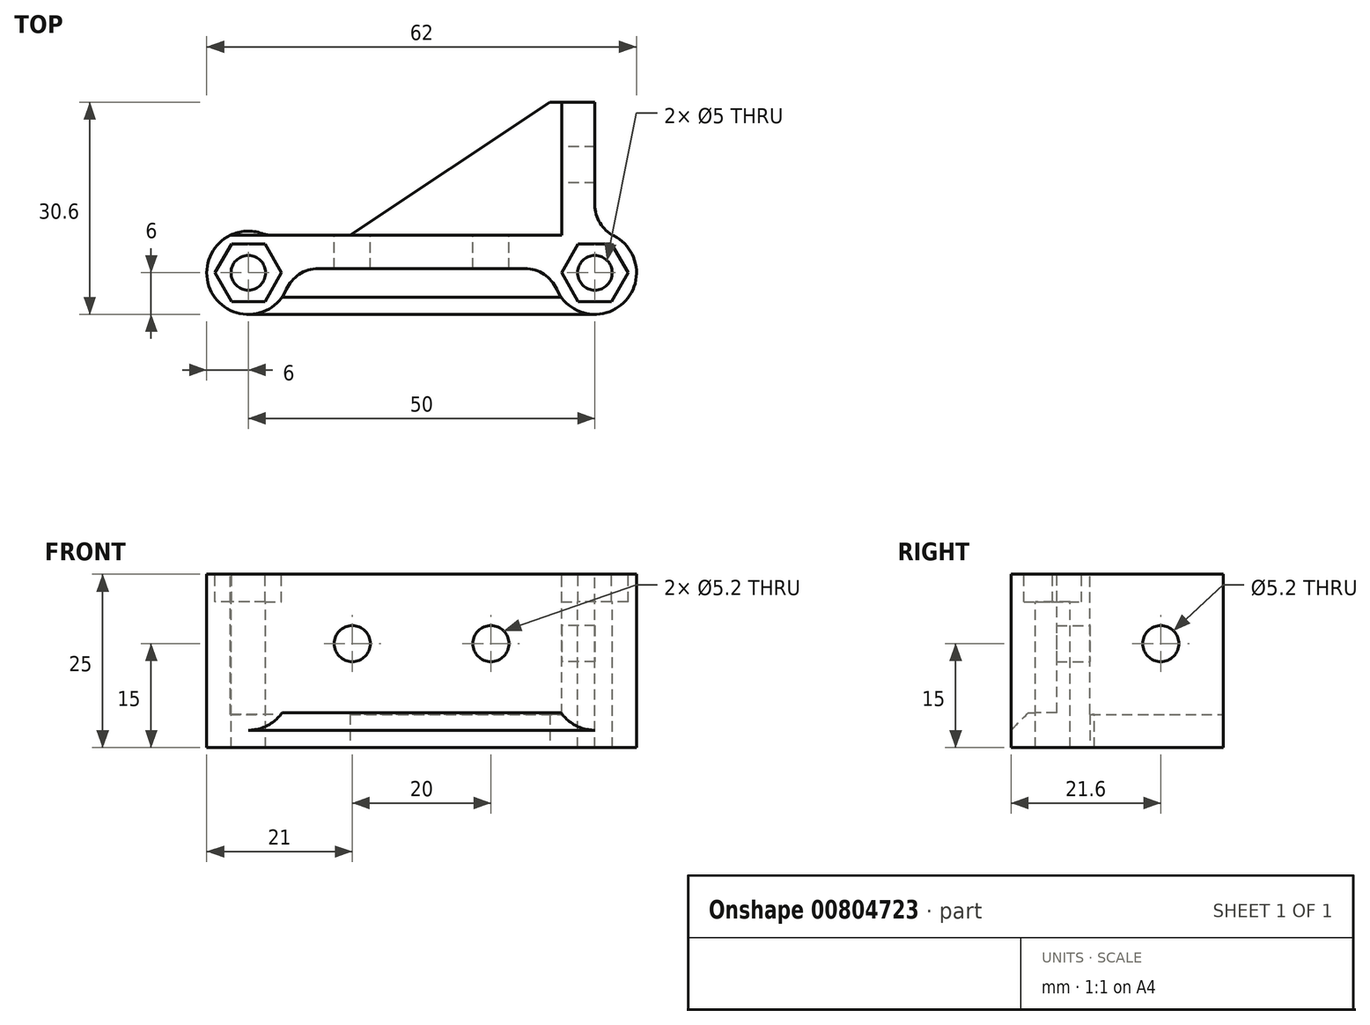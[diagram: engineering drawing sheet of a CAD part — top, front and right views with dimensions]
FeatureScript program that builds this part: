
annotation { "Feature Type Name" : "Feature", "Feature Type Description" : "" }
export const myFeature = defineFeature(function(context is Context, id is Id, definition is map)
    precondition{}
    {
        {
            var Q0;
            Q0=qCreatedBy(makeId("Top.planeOp"),FACE);
            var sketch = newSketch(context, id + "F0", { "sketchPlane" : qUnion([Q0])});
            skCircle(sketch, "E0", {"center": v(-25, 0) * mm, "radius": 2.5 * mm});
            skArc(sketch, "E1", {"start": v(-23.05, 5.67) * mm, "mid": v(-30.5, -2.41) * mm, "end": v(-19.5, -2.4) * mm});
            skCircle(sketch, "E2", {"center": v(25, 0) * mm, "radius": 2.5 * mm});
            skArc(sketch, "E3", {"start": v(19.5, -2.4) * mm, "mid": v(29.11, -4.37) * mm, "end": v(27.73, 5.34) * mm});
            skLineSegment(sketch, "E4", {"start": v(-21.42, 5.4) * mm, "end": v(20.2, 5.4) * mm});
            skLineSegment(sketch, "E5", {"start": v(-14.92, 0.6) * mm, "end": v(14.92, 0.6) * mm});
            skArc(sketch, "E6", {"start": v(-14.92, 0.6) * mm, "mid": v(-17.66, -0.22) * mm, "end": v(-19.5, -2.4) * mm});
            skArc(sketch, "E7", {"start": v(14.92, 0.6) * mm, "mid": v(17.66, -0.22) * mm, "end": v(19.5, -2.4) * mm});
            skLineSegment(sketch, "E8", {"start": v(20.2, 5.4) * mm, "end": v(20.2, 24.6) * mm});
            skLineSegment(sketch, "E9", {"start": v(20.2, 24.6) * mm, "end": v(25, 24.6) * mm});
            skLineSegment(sketch, "E10", {"start": v(25, 24.6) * mm, "end": v(25, 9.8) * mm});
            skArc(sketch, "E11", {"start": v(25, 9.8) * mm, "mid": v(25.74, 7.19) * mm, "end": v(27.73, 5.34) * mm});
            skLineSegment(sketch, "E12", {"start": v(-25, 0) * mm, "end": v(25, 0) * mm, "construction": true});
            skPoint(sketch, "E13.visualSharp", {"position": v(-22.38, 5.4) * mm});
            skArc(sketch, "E13.filletArc", {"start": v(-23.05, 5.67) * mm, "mid": v(-22.24, 5.47) * mm, "end": v(-21.42, 5.4) * mm});
            skSolve(sketch);
        }
        {
            var Q0;
            Q0=qSketchRegion(id+"F0",true);
            extrude(context, id + "F1", {"entities" : qUnion([Q0]), "oppositeDirection" : true, "depth" : 25 * mm, "offsetDistance" : 25 * mm});
        }
        {
            var Q0;
            Q0=makeQuery(id+"F1.opExtrude","CAP_FACE",FACE,{"disambiguationData":[OSD([sQuery(id+"F0.wireOp",EDGE,"E0"),sQuery(id+"F0.wireOp",EDGE,"E1"),sQuery(id+"F0.wireOp",EDGE,"E2"),sQuery(id+"F0.wireOp",EDGE,"E3"),sQuery(id+"F0.wireOp",EDGE,"E4"),sQuery(id+"F0.wireOp",EDGE,"E5"),sQuery(id+"F0.wireOp",EDGE,"E6"),sQuery(id+"F0.wireOp",EDGE,"E7"),sQuery(id+"F0.wireOp",EDGE,"E8"),sQuery(id+"F0.wireOp",EDGE,"E9"),sQuery(id+"F0.wireOp",EDGE,"E10"),sQuery(id+"F0.wireOp",EDGE,"E11")])],"isStart":true});
            var sketch = newSketch(context, id + "F2", { "sketchPlane" : qUnion([Q0])});
            skCircle(sketch, "E14.cCircle", {"center": v(25, 0) * mm, "radius": 4.16 * mm, "construction": true});
            skLineSegment(sketch, "E14.0", {"start": v(20.2, 0) * mm, "end": v(22.6, 4.16) * mm});
            skLineSegment(sketch, "E14.1", {"start": v(22.6, 4.16) * mm, "end": v(27.4, 4.16) * mm});
            skLineSegment(sketch, "E14.2", {"start": v(27.4, 4.16) * mm, "end": v(29.8, 0) * mm});
            skLineSegment(sketch, "E14.3", {"start": v(29.8, 0) * mm, "end": v(27.4, -4.16) * mm});
            skLineSegment(sketch, "E14.4", {"start": v(27.4, -4.16) * mm, "end": v(22.6, -4.16) * mm});
            skLineSegment(sketch, "E14.5", {"start": v(22.6, -4.16) * mm, "end": v(20.2, 0) * mm});
            skPoint(sketch, "E14.0.midPoint", {"position": v(21.4, 2.08) * mm});
            skLineSegment(sketch, "E15", {"start": v(0, 0.6) * mm, "end": v(0, -5.53) * mm, "construction": true});
            skLineSegment(sketch, "E16.MirrorCS", {"start": v(-27.4, 4.16) * mm, "end": v(-29.8, 0) * mm});
            skLineSegment(sketch, "E17.MirrorCS", {"start": v(-22.6, 4.16) * mm, "end": v(-27.4, 4.16) * mm});
            skLineSegment(sketch, "E18.MirrorCS", {"start": v(-20.2, 0) * mm, "end": v(-22.6, 4.16) * mm});
            skLineSegment(sketch, "E19.MirrorCS", {"start": v(-22.6, -4.16) * mm, "end": v(-20.2, 0) * mm});
            skLineSegment(sketch, "E20.MirrorCS", {"start": v(-27.4, -4.16) * mm, "end": v(-22.6, -4.16) * mm});
            skLineSegment(sketch, "E21.MirrorCS", {"start": v(-29.8, 0) * mm, "end": v(-27.4, -4.16) * mm});
            skSolve(sketch);
        }
        {
            var Q0;
            Q0=qSketchRegion(id+"F2",true);
            extrude(context, id + "F3", {"entities" : qUnion([Q0]), "operationType" : NewBodyOperationType.REMOVE, "oppositeDirection" : true, "depth" : 4 * mm, "offsetDistance" : 25 * mm});
        }
        {
            var Q0;
            Q0=makeQuery(id+"F1.opExtrude","CAP_FACE",FACE,{"disambiguationData":[OSD([sQuery(id+"F0.wireOp",EDGE,"E0"),sQuery(id+"F0.wireOp",EDGE,"E1"),sQuery(id+"F0.wireOp",EDGE,"E2"),sQuery(id+"F0.wireOp",EDGE,"E3"),sQuery(id+"F0.wireOp",EDGE,"E4"),sQuery(id+"F0.wireOp",EDGE,"E5"),sQuery(id+"F0.wireOp",EDGE,"E6"),sQuery(id+"F0.wireOp",EDGE,"E7"),sQuery(id+"F0.wireOp",EDGE,"E8"),sQuery(id+"F0.wireOp",EDGE,"E9"),sQuery(id+"F0.wireOp",EDGE,"E10"),sQuery(id+"F0.wireOp",EDGE,"E11"),sQuery(id+"F0.wireOp",EDGE,"E13.filletArc")])],"isStart":false});
            var sketch = newSketch(context, id + "F4", { "sketchPlane" : qUnion([Q0])});
            skLineSegment(sketch, "E22", {"start": v(20.2, -24.6) * mm, "end": v(18.5, -24.6) * mm});
            skLineSegment(sketch, "E23", {"start": v(18.5, -24.6) * mm, "end": v(-10.3, -5.4) * mm});
            skLineSegment(sketch, "E24", {"start": v(-10.3, -5.4) * mm, "end": v(20.2, -5.4) * mm});
            skLineSegment(sketch, "E25", {"start": v(20.2, -5.4) * mm, "end": v(20.2, -24.6) * mm});
            skSolve(sketch);
        }
        {
            var Q0;
            Q0=qSketchRegion(id+"F4",true);
            extrude(context, id + "F5", {"entities" : qUnion([Q0]), "operationType" : NewBodyOperationType.ADD, "oppositeDirection" : true, "depth" : 4.8 * mm, "offsetDistance" : 25 * mm});
        }
        {
            var Q0;
            Q0=makeQuery(id+"F1.opExtrude","SWEPT_FACE",FACE,{"disambiguationData":[OSD([sQuery(id+"F0.wireOp",EDGE,"E4")])]});
            var sketch = newSketch(context, id + "F6", { "sketchPlane" : qUnion([Q0])});
            skCircle(sketch, "E26", {"center": v(-10, -10) * mm, "radius": 2.6 * mm});
            skCircle(sketch, "E27", {"center": v(10, -10) * mm, "radius": 2.6 * mm});
            skLineSegment(sketch, "E28", {"start": v(-10, -10) * mm, "end": v(10, -10) * mm, "construction": true});
            skSolve(sketch);
        }
        {
            var Q0;
            Q0=qSketchRegion(id+"F6",true);
            extrude(context, id + "F7", {"entities" : qUnion([Q0]), "operationType" : NewBodyOperationType.REMOVE, "endBound" : BoundingType.UP_TO_NEXT, "oppositeDirection" : true, "depth" : 25 * mm, "offsetDistance" : 25 * mm});
        }
        {
            var Q0;
            Q0=makeQuery(id+"F1.opExtrude","SWEPT_FACE",FACE,{"disambiguationData":[OSD([sQuery(id+"F0.wireOp",EDGE,"E8")])]});
            var sketch = newSketch(context, id + "F8", { "sketchPlane" : qUnion([Q0])});
            skLineSegment(sketch, "E29", {"start": v(-24.6, -10) * mm, "end": v(-15.6, -10) * mm, "construction": true});
            skLineSegment(sketch, "E30", {"start": v(-15.6, -10) * mm, "end": v(-15.6, 0) * mm, "construction": true});
            skCircle(sketch, "E31", {"center": v(-15.6, -10) * mm, "radius": 2.6 * mm});
            skSolve(sketch);
        }
        {
            var Q0;
            Q0=qSketchRegion(id+"F8",true);
            extrude(context, id + "F9", {"entities" : qUnion([Q0]), "operationType" : NewBodyOperationType.REMOVE, "endBound" : BoundingType.UP_TO_NEXT, "oppositeDirection" : true, "depth" : 25 * mm, "offsetDistance" : 25 * mm});
        }
        {
            var Q0;
            Q0=qCreatedBy(makeId("Right.planeOp"),FACE);
            var sketch = newSketch(context, id + "F10", { "sketchPlane" : qUnion([Q0])});
            skLineSegment(sketch, "E32", {"start": v(0.6, -20) * mm, "end": v(0.6, -25) * mm});
            skLineSegment(sketch, "E33", {"start": v(0.6, -25) * mm, "end": v(-6, -25) * mm});
            skLineSegment(sketch, "E34", {"start": v(-6, -25) * mm, "end": v(-6, -22.5) * mm});
            skLineSegment(sketch, "E35", {"start": v(-6, -22.5) * mm, "end": v(-3.5, -20) * mm});
            skLineSegment(sketch, "E36", {"start": v(-3.5, -20) * mm, "end": v(0.6, -20) * mm});
            skPoint(sketch, "E37.orphan", {"position": v(0.6, 0) * mm});
            skLineSegment(sketch, "E38.0.2", {"start": v(-6, -25) * mm, "end": v(5.34, -25) * mm, "construction": true});
            skSolve(sketch);
        }
        {
            var Q0;
            Q0=qSketchRegion(id+"F10",true);
            extrude(context, id + "F11", {"entities" : qUnion([Q0]), "operationType" : NewBodyOperationType.ADD, "endBound" : BoundingType.UP_TO_NEXT, "depth" : 25 * mm, "offsetDistance" : 25 * mm, "hasSecondDirection" : true, "secondDirectionBound" : SecondDirectionBoundingType.UP_TO_NEXT, "secondDirectionOppositeDirection" : true, "secondDirectionDepth" : 25 * mm});
        }
        {
            var Q0;
            Q0=makeQuery(id+"F1.opExtrude","CAP_FACE",FACE,{"disambiguationData":[OSD([sQuery(id+"F0.wireOp",EDGE,"E0"),sQuery(id+"F0.wireOp",EDGE,"E1"),sQuery(id+"F0.wireOp",EDGE,"E2"),sQuery(id+"F0.wireOp",EDGE,"E3"),sQuery(id+"F0.wireOp",EDGE,"E4"),sQuery(id+"F0.wireOp",EDGE,"E5"),sQuery(id+"F0.wireOp",EDGE,"E6"),sQuery(id+"F0.wireOp",EDGE,"E7"),sQuery(id+"F0.wireOp",EDGE,"E8"),sQuery(id+"F0.wireOp",EDGE,"E9"),sQuery(id+"F0.wireOp",EDGE,"E10"),sQuery(id+"F0.wireOp",EDGE,"E11"),sQuery(id+"F0.wireOp",EDGE,"E13.filletArc")])],"isStart":true});
            var sketch = newSketch(context, id + "F12", { "sketchPlane" : qUnion([Q0])});
            skLineSegment(sketch, "E39.bottom", {"start": v(-21.42, 5.4) * mm, "end": v(-27.62, 5.4) * mm});
            skLineSegment(sketch, "E39.top", {"start": v(-21.42, 8.4) * mm, "end": v(-27.62, 8.4) * mm});
            skLineSegment(sketch, "E39.left", {"start": v(-21.42, 5.4) * mm, "end": v(-21.42, 8.4) * mm});
            skLineSegment(sketch, "E39.right", {"start": v(-27.62, 5.4) * mm, "end": v(-27.62, 8.4) * mm});
            skSolve(sketch);
        }
        {
            var Q0;
            Q0=qSketchRegion(id+"F12",true);
            var Q1;
            Q1=makeQuery(id+"F5.opExtrude","CAP_FACE",FACE,{"disambiguationData":[OSD([sQuery(id+"F4.wireOp",EDGE,"E22"),sQuery(id+"F4.wireOp",EDGE,"E23"),sQuery(id+"F4.wireOp",EDGE,"E24"),sQuery(id+"F4.wireOp",EDGE,"E25")])],"isStart":false});
            extrude(context, id + "F13", {"entities" : qUnion([Q0]), "operationType" : NewBodyOperationType.REMOVE, "endBound" : BoundingType.UP_TO_SURFACE, "oppositeDirection" : true, "depth" : 25 * mm, "endBoundEntityFace" : qUnion([Q1]), "offsetDistance" : 25 * mm});
        }
    });
